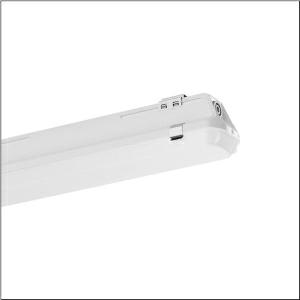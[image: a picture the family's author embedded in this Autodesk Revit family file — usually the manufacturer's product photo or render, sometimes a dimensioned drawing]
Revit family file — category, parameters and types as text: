
# Revit family: monsun_r__11_51fp11mp4b0q_bcda
name_source: partatom
category: Lighting Fixtures
units: mm (PartAtom-declared; Revit-internal decimal feet)

## family parameters
Cut with Voids When Loaded = No
Host = Face
Light Source = No
Part Type = Normal
Room Calculation Point = No
Round Connector Dimension = Use Diameter
Shared = No

## types (1)
- --- (1 x LED, 11900 lm, 66.2 W, 4000K)
    Apparent Load = 66 VA
    CIE Flux Codes = 71 88 97 97 100
    Color Rendering = 80
    Color Temperature = 4000K
    Default Elevation = 1800 mm
    Description = Monsun® 11, damp-proof luminaire, chain hanger, primary optical cover: enclosure, of PMMA, light emission: direct distribution, primary light characteristic: symmetric, installation type: suspended mounting, surface-mounted, horizontal mounting, vertical mounting, LED, rated luminous flux: 11.900lm, luminous efficacy: 180lm/W, light colour: 840, colour temperature: 4000K, control gear: ECG, with terminal, 3-pole, max. 2.5mm², mains connection: 220..240V, AC, 50/60Hz, rated input power: 66W, luminaire housing, of glass-fibre reinforced polyester, uncoated, bright grey, incl. chain hanger, length: 1.590mm, width: 90mm, height: 88mm, clip for enclosure, of stainless steel (V2A), ceiling mounting element, of stainless steel (V2A), chain hanger, of stainless steel (V2A), protection rating (complete): IP66, insulation class (complete): insulation class I (protective earthing), certification: CE, ENEC, VDE, UKCA, protection symbol: D, impact resistance: IK04, permissible operating ambient temperature: -35..+35°C, standard: EN 50419, EN 60598-2-1, no direct snow, no direct sun, no direct rain, for indoor or canopied outdoor use, corresponds to IFS (International Featured Standards) requirements for safety and quality in the food industry, contact your sales advisor before using the luminaires in applications with unclear chemical exposure, large temperature fluctuations or condensation-forming humidity, LABS conformity tested according to VDMA 24364:2018-05, packaging unit: 1 piece
    Height = 89 mm
    Lamp = 1 x LED
    Lamp Light Flux = 11900 lm
    Lamp Power = 66.2 W
    Lamp count = 1
    Length = 1590 mm
    Luminous efficacy = 180 lm/W
    Manufacturer = Siteco
    ModVariant = No
    Model = 51FP11MP4B0Q
    Mounting Place = Ceiling
    Mounting Type = Surface mounted
    Number of Poles = 1
    OnlyDefault = Yes
    Power Factor = 1
    Product Name = Monsun® 11
    Product group = damp-proof luminaire
    ProductGroupID = 300
    Protection Class = Protection class I
    Protection Degree = IP 66
    RLX_Detail_Level = 1
    RLX_Emergency_Light_Flux = 0 lm
    RLX_Emergency_Type = 0
    RLX_Emergency_Type_DB = No
    RlxData = <blob elided: 90117 chars, md5=47b5e0d3>
    Socket = socket
    Standby Power = 0 W
    System Light Flux = 11900 lm
    System Power = 66 W
    Type Comments = factory setting: luminous flux: 100 % | (A | C | E) | 155 mA
    Type Image = l_1004748.jpg
    URL = http://relux.com
    VarID = @adj_142017
    Voltage = 0 V
    Weight = 0.00 kg
    Width = 90 mm

## geometry (parser evidence)
native form markers: Blend x4, Sweep x9
no freeform markers — native parametric forms only
